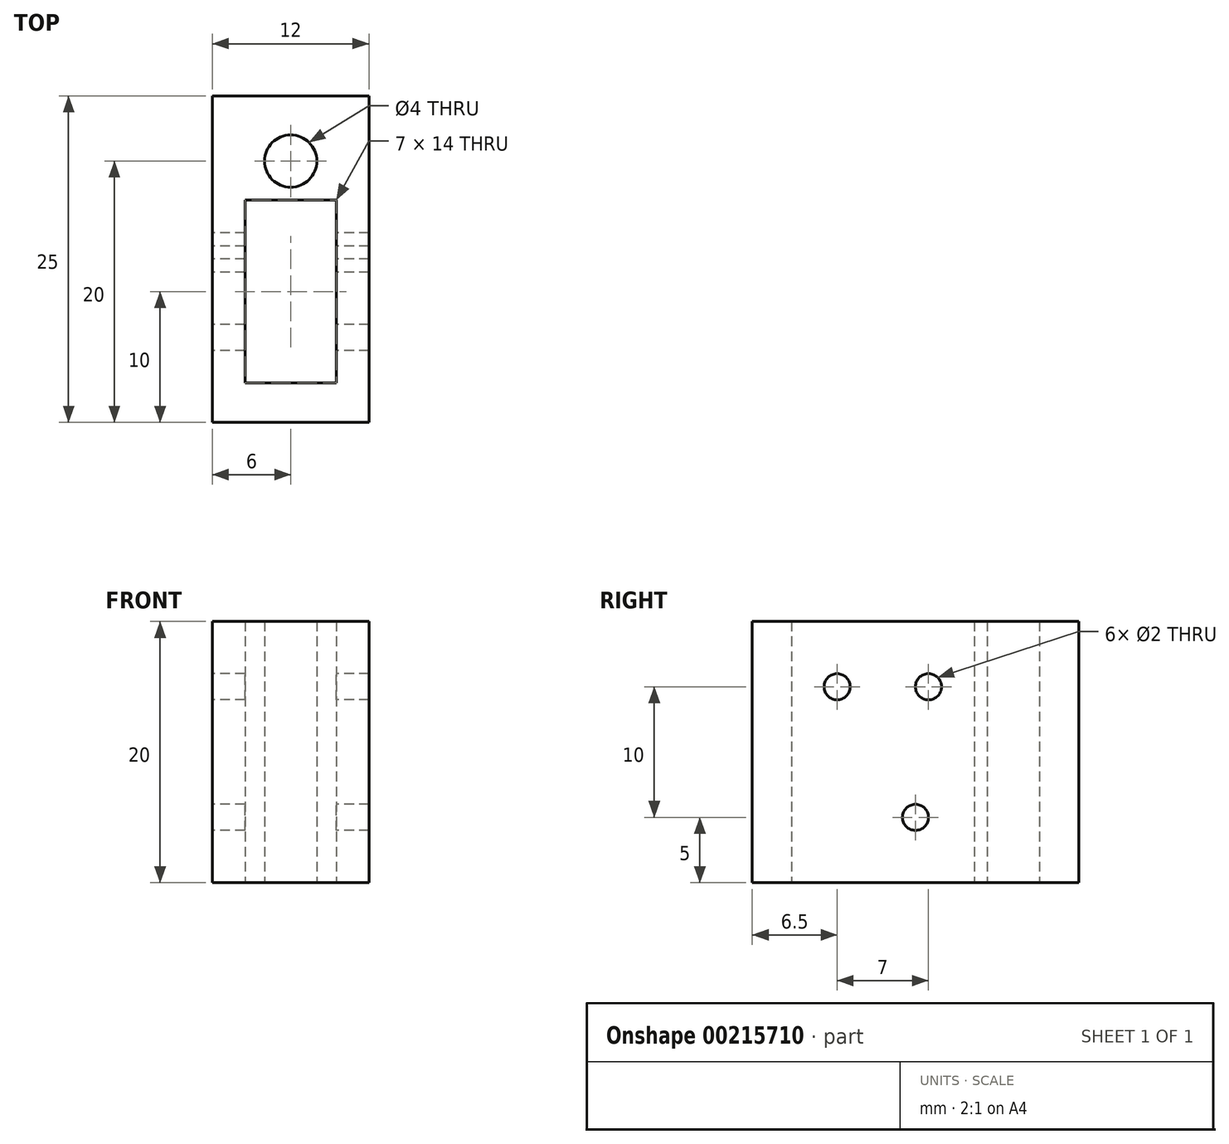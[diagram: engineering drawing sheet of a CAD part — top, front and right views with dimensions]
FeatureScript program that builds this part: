
annotation { "Feature Type Name" : "Feature", "Feature Type Description" : "" }
export const myFeature = defineFeature(function(context is Context, id is Id, definition is map)
    precondition{}
    {
        {
            var Q0;
            Q0=qCreatedBy(makeId("Top.planeOp"),FACE);
            var sketch = newSketch(context, id + "F0", { "sketchPlane" : qUnion([Q0])});
            skLineSegment(sketch, "E0.bottom", {"start": v(-6, 5) * mm, "end": v(6, 5) * mm});
            skLineSegment(sketch, "E0.top", {"start": v(-6, -20) * mm, "end": v(6, -20) * mm});
            skLineSegment(sketch, "E0.left", {"start": v(-6, 5) * mm, "end": v(-6, -20) * mm});
            skLineSegment(sketch, "E0.right", {"start": v(6, 5) * mm, "end": v(6, -20) * mm});
            skCircle(sketch, "E1", {"center": v(0, 0) * mm, "radius": 2 * mm});
            skLineSegment(sketch, "E2.bottom", {"start": v(-3.5, -3) * mm, "end": v(3.5, -3) * mm});
            skLineSegment(sketch, "E2.top", {"start": v(-3.5, -17) * mm, "end": v(3.5, -17) * mm});
            skLineSegment(sketch, "E2.left", {"start": v(-3.5, -3) * mm, "end": v(-3.5, -17) * mm});
            skLineSegment(sketch, "E2.right", {"start": v(3.5, -3) * mm, "end": v(3.5, -17) * mm});
            skSolve(sketch);
        }
        {
            var Q0;
            Q0 = qSketchRegion(id + "F0", true);
            extrude(context, id + "F1", {"entities" : qUnion([Q0]), "depth" : 20 * mm});
        }
        {
            var Q0;
            Q0=makeQuery(id+"F1.opExtrude","SWEPT_FACE",FACE,{"disambiguationData":[OSD([sQuery(id+"F0.wireOp",EDGE,"E0.left")])]});
            var sketch = newSketch(context, id + "F2", { "sketchPlane" : qUnion([Q0])});
            skLineSegment(sketch, "E3", {"start": v(-5, 15) * mm, "end": v(20, 15) * mm, "construction": true});
            skCircle(sketch, "E4", {"center": v(13.5, 15) * mm, "radius": 1 * mm});
            skCircle(sketch, "E5", {"center": v(6.5, 15) * mm, "radius": 1 * mm});
            skCircle(sketch, "E6", {"center": v(7.5, 5) * mm, "radius": 1 * mm});
            skPoint(sketch, "E6.centerSnap0", {"position": v(7.5, 15) * mm});
            skSolve(sketch);
        }
        {
            var Q0;
            Q0 = qSketchRegion(id + "F2", true);
            extrude(context, id + "F3", {"entities" : qUnion([Q0]), "operationType" : NewBodyOperationType.REMOVE, "endBound" : BoundingType.THROUGH_ALL, "oppositeDirection" : true, "depth" : 25 * mm});
        }
    });
